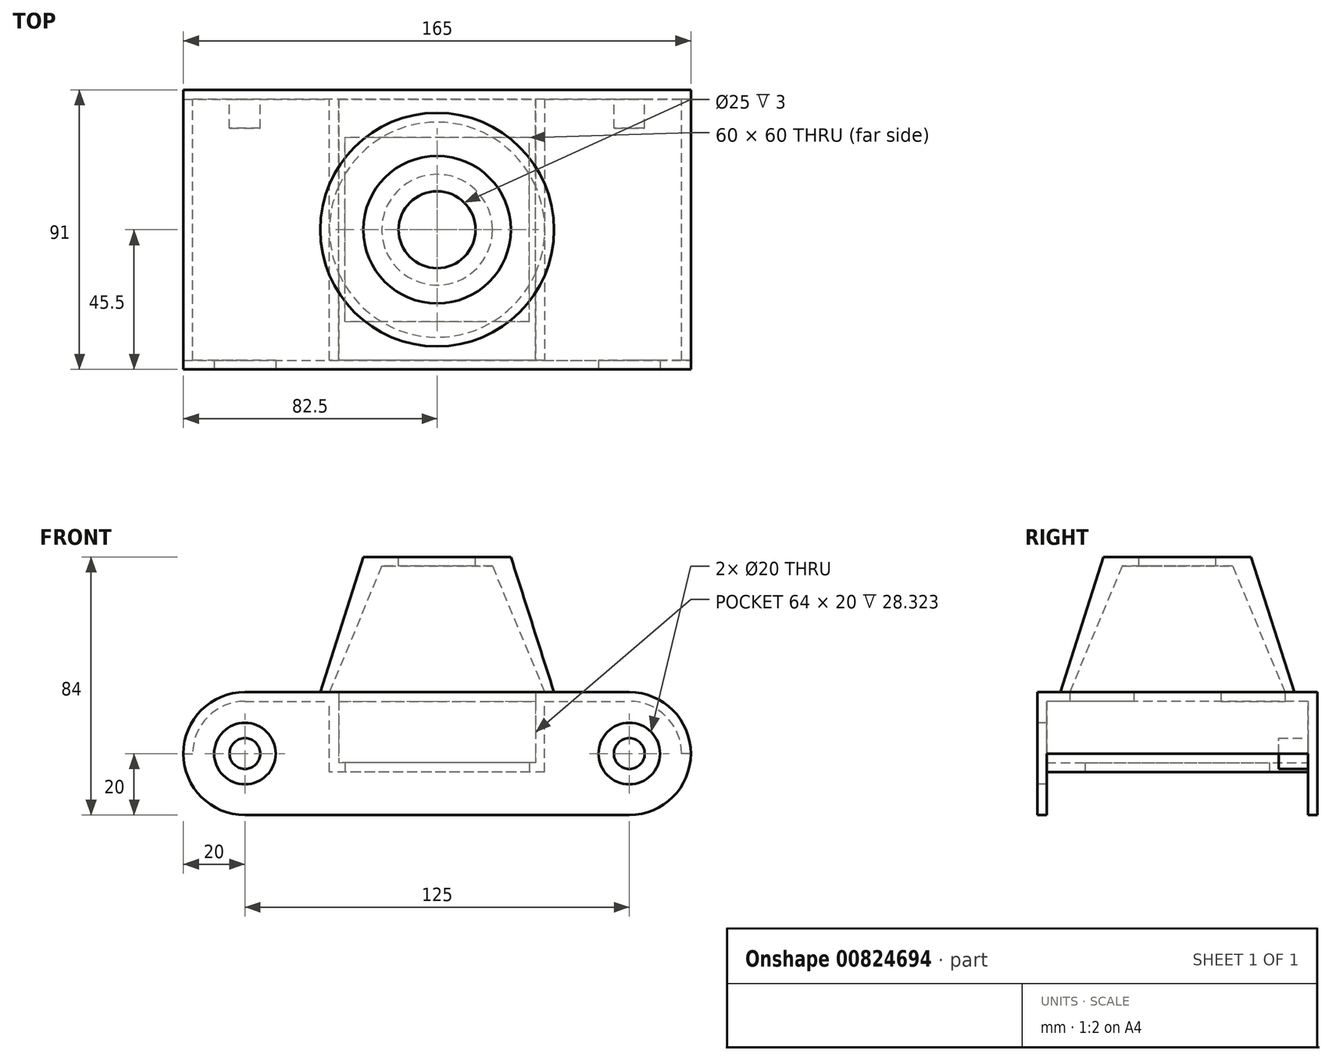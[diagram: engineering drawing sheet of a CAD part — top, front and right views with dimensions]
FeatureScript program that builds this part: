
annotation { "Feature Type Name" : "Feature", "Feature Type Description" : "" }
export const myFeature = defineFeature(function(context is Context, id is Id, definition is map)
    precondition{}
    {
        {
            var Q0;
            Q0=qCreatedBy(makeId("Front.planeOp"),FACE);
            var sketch = newSketch(context, id + "F0", { "sketchPlane" : qUnion([Q0])});
            skLineSegment(sketch, "E0.bottom", {"start": v(62.5, 20) * mm, "end": v(-62.5, 20) * mm});
            skLineSegment(sketch, "E0.top", {"start": v(62.5, -20) * mm, "end": v(-62.5, -20) * mm});
            skLineSegment(sketch, "E0.left", {"start": v(62.5, 20) * mm, "end": v(62.5, -20) * mm});
            skLineSegment(sketch, "E0.right", {"start": v(-62.5, 20) * mm, "end": v(-62.5, -20) * mm});
            skPoint(sketch, "E0.middle", {"position": v(0, 0) * mm});
            skArc(sketch, "E1", {"start": v(-62.5, 20) * mm, "mid": v(-82.5, 0) * mm, "end": v(-62.5, -20) * mm});
            skArc(sketch, "E2", {"start": v(62.5, -20) * mm, "mid": v(82.5, 0) * mm, "end": v(62.5, 20) * mm});
            skSolve(sketch);
        }
        {
            var Q0;
            Q0 = qSketchRegion(id + "F0", true);
            extrude(context, id + "F1", {"entities" : qUnion([Q0]), "depth" : 3 * mm, "offsetDistance" : 25 * mm});
        }
        {
            var Q0;
            Q0=makeQuery(id+"F1.opExtrude","CAP_FACE",FACE,{"disambiguationData":[OSD([sQuery(id+"F0.wireOp",EDGE,"E0.bottom"),sQuery(id+"F0.wireOp",EDGE,"E0.top"),sQuery(id+"F0.wireOp",EDGE,"E1"),sQuery(id+"F0.wireOp",EDGE,"E2")])],"isStart":false});
            var sketch = newSketch(context, id + "F2", { "sketchPlane" : qUnion([Q0])});
            skLineSegment(sketch, "E3.bottom", {"start": v(-62.5, 20) * mm, "end": v(62.5, 20) * mm});
            skLineSegment(sketch, "E3.top", {"start": v(-62.5, 17) * mm, "end": v(62.5, 17) * mm});
            skLineSegment(sketch, "E3.left", {"start": v(-62.5, 20) * mm, "end": v(-62.5, 17) * mm});
            skLineSegment(sketch, "E3.right", {"start": v(62.5, 20) * mm, "end": v(62.5, 17) * mm});
            skLineSegment(sketch, "E4", {"start": v(-82.5, 0) * mm, "end": v(-79.5, 0) * mm});
            skLineSegment(sketch, "E5", {"start": v(82.5, 0) * mm, "end": v(79.5, 0) * mm});
            skArc(sketch, "E6", {"start": v(-62.5, 20) * mm, "mid": v(-76.64, 14.14) * mm, "end": v(-82.5, 0) * mm});
            skArc(sketch, "E7", {"start": v(-62.5, 17) * mm, "mid": v(-74.52, 12.02) * mm, "end": v(-79.5, 0) * mm});
            skArc(sketch, "E8", {"start": v(82.5, 0) * mm, "mid": v(76.64, 14.14) * mm, "end": v(62.5, 20) * mm});
            skArc(sketch, "E9", {"start": v(79.5, 0) * mm, "mid": v(74.52, 12.02) * mm, "end": v(62.5, 17) * mm});
            skSolve(sketch);
        }
        {
            var Q0;
            Q0 = qSketchRegion(id + "F2", true);
            extrude(context, id + "F3", {"entities" : qUnion([Q0]), "operationType" : NewBodyOperationType.ADD, "depth" : 85 * mm, "offsetDistance" : 25 * mm});
        }
        {
            var Q0;
            Q0=makeQuery(id+"F3.opExtrude","CAP_FACE",FACE,{"disambiguationData":[OSD([sQuery(id+"F2.wireOp",EDGE,"E3.bottom"),sQuery(id+"F2.wireOp",EDGE,"E3.top"),sQuery(id+"F2.wireOp",EDGE,"E4"),sQuery(id+"F2.wireOp",EDGE,"E5"),sQuery(id+"F2.wireOp",EDGE,"E6"),sQuery(id+"F2.wireOp",EDGE,"E7"),sQuery(id+"F2.wireOp",EDGE,"E8"),sQuery(id+"F2.wireOp",EDGE,"E9")])],"isStart":false});
            var sketch = newSketch(context, id + "F4", { "sketchPlane" : qUnion([Q0])});
            skLineSegment(sketch, "E10.bottom", {"start": v(-62.5, 20) * mm, "end": v(62.5, 20) * mm});
            skLineSegment(sketch, "E10.top", {"start": v(-62.5, -20) * mm, "end": v(62.5, -20) * mm});
            skLineSegment(sketch, "E10.left", {"start": v(-62.5, 20) * mm, "end": v(-62.5, -20) * mm});
            skLineSegment(sketch, "E10.right", {"start": v(62.5, 20) * mm, "end": v(62.5, -20) * mm});
            skArc(sketch, "E11", {"start": v(-62.5, 20) * mm, "mid": v(-82.5, 0) * mm, "end": v(-62.5, -20) * mm});
            skArc(sketch, "E12", {"start": v(62.5, -20) * mm, "mid": v(82.5, 0) * mm, "end": v(62.5, 20) * mm});
            skSolve(sketch);
        }
        {
            var Q0;
            Q0 = qSketchRegion(id + "F4", true);
            extrude(context, id + "F5", {"entities" : qUnion([Q0]), "operationType" : NewBodyOperationType.ADD, "depth" : 3 * mm, "offsetDistance" : 25 * mm});
        }
        {
            var Q0;
            Q0=makeQuery(id+"F3.opExtrude","SWEPT_FACE",FACE,{"disambiguationData":[OSD([sQuery(id+"F2.wireOp",EDGE,"E3.top")])]});
            var sketch = newSketch(context, id + "F6", { "sketchPlane" : qUnion([Q0])});
            skLineSegment(sketch, "E13", {"start": v(-62.5, 88) * mm, "end": v(62.5, 3) * mm, "construction": true});
            skCircle(sketch, "E14", {"center": v(0, 45.5) * mm, "radius": 35 * mm});
            skSolve(sketch);
        }
        {
            var Q0;
            Q0 = qSketchRegion(id + "F6", true);
            extrude(context, id + "F7", {"entities" : qUnion([Q0]), "operationType" : NewBodyOperationType.REMOVE, "oppositeDirection" : true, "depth" : 25 * mm, "offsetDistance" : 25 * mm});
        }
        {
            var Q0;
            Q0=makeQuery(id+"F5.boolean.opBoolean","MERGE",FACE,{"derivedFrom":[makeQuery(id+"F3.boolean.opBoolean","MERGE",FACE,{"derivedFrom":[makeQuery(id+"F1.opExtrude","SWEPT_FACE",FACE,{"disambiguationData":[OSD([sQuery(id+"F0.wireOp",EDGE,"E0.bottom")])]}),makeQuery(id+"F3.opExtrude","SWEPT_FACE",FACE,{"disambiguationData":[OSD([sQuery(id+"F2.wireOp",EDGE,"E3.bottom")])]})]}),makeQuery(id+"F5.opExtrude","SWEPT_FACE",FACE,{"disambiguationData":[OSD([sQuery(id+"F4.wireOp",EDGE,"E10.bottom")])]})]});
            var sketch = newSketch(context, id + "F8", { "sketchPlane" : qUnion([Q0])});
            skCircle(sketch, "E15", {"center": v(0, -45.5) * mm, "radius": 38 * mm});
            skSolve(sketch);
        }
        {
            var Q0;
            Q0=makeQuery(id+"F8.imprint","IMPRINT",FACE,{"disambiguationData":[TD([[makeQuery(id+"F8.imprint","IMPRINT",EDGE,{"derivedFrom":sQuery(id+"F8.wireOp",EDGE,"E15")}),-1.0]])]});
            cPlane(context, id + "F9", {"entities" : qUnion([Q0]), "cplaneType" : CPlaneType.OFFSET, "offset" : 44 * mm, "width" : 150 * mm, "height" : 150 * mm});
        }
        {
            var Q0;
            Q0=qCreatedBy(id+"F9.planeOp",FACE);
            var sketch = newSketch(context, id + "F10", { "sketchPlane" : qUnion([Q0])});
            skCircle(sketch, "E16", {"center": v(0, -45.5) * mm, "radius": 24 * mm});
            skSolve(sketch);
        }
        {
            var Q1;
            Q1 = qSketchRegion(id + "F10", true);
            var Q2;
            Q2 = qSketchRegion(id + "F8", true);
            loft(context, id + "F11", {"operationType" : NewBodyOperationType.ADD, "sheetProfilesArray" : [{ "sheetProfileEntities" : qUnion([Q1]) }, { "sheetProfileEntities" : qUnion([Q2]) }]});
        }
        {
            var Q0;
            Q0=makeQuery(id+"F11.opLoft","CAP_FACE",FACE,{"disambiguationData":[OSD([makeQuery(id+"F10.imprint","IMPRINT",FACE,{"disambiguationData":[TD([[makeQuery(id+"F10.imprint","IMPRINT",EDGE,{"derivedFrom":sQuery(id+"F10.wireOp",EDGE,"E16")}),1.0]])]})])],"isStart":true});
            var sketch = newSketch(context, id + "F12", { "sketchPlane" : qUnion([Q0])});
            skCircle(sketch, "E17", {"center": v(0, -45.5) * mm, "radius": 12.5 * mm});
            skSolve(sketch);
        }
        {
            var Q0;
            Q0 = qSketchRegion(id + "F12", true);
            extrude(context, id + "F13", {"entities" : qUnion([Q0]), "operationType" : NewBodyOperationType.REMOVE, "oppositeDirection" : true, "depth" : 70.6 * mm, "offsetDistance" : 25 * mm});
        }
        {
            var Q0;
            Q0=makeQuery(id+"F5.boolean.opBoolean","MERGE",FACE,{"derivedFrom":[makeQuery(id+"F3.boolean.opBoolean","MERGE",FACE,{"derivedFrom":[makeQuery(id+"F1.opExtrude","SWEPT_FACE",FACE,{"disambiguationData":[OSD([sQuery(id+"F0.wireOp",EDGE,"E0.bottom")])]}),makeQuery(id+"F3.opExtrude","SWEPT_FACE",FACE,{"disambiguationData":[OSD([sQuery(id+"F2.wireOp",EDGE,"E3.bottom")])]})]}),makeQuery(id+"F5.opExtrude","SWEPT_FACE",FACE,{"disambiguationData":[OSD([sQuery(id+"F4.wireOp",EDGE,"E10.bottom")])]})]});
            var sketch = newSketch(context, id + "F14", { "sketchPlane" : qUnion([Q0])});
            skCircle(sketch, "E18", {"center": v(0, -45.5) * mm, "radius": 35 * mm});
            skSolve(sketch);
        }
        {
            var Q0;
            Q0=qCreatedBy(id+"F9.planeOp",FACE);
            cPlane(context, id + "F15", {"entities" : qUnion([Q0]), "cplaneType" : CPlaneType.OFFSET, "offset" : 3 * mm, "oppositeDirection" : true, "width" : 150 * mm, "height" : 150 * mm});
        }
        {
            var Q0;
            Q0=qCreatedBy(id+"F15.planeOp",FACE);
            var sketch = newSketch(context, id + "F16", { "sketchPlane" : qUnion([Q0])});
            skCircle(sketch, "E19", {"center": v(0, -45.5) * mm, "radius": 18 * mm});
            skSolve(sketch);
        }
        {
            var Q1;
            Q1 = qSketchRegion(id + "F16", true);
            var Q2;
            Q2 = qSketchRegion(id + "F14", true);
            loft(context, id + "F17", {"operationType" : NewBodyOperationType.REMOVE, "sheetProfilesArray" : [{ "sheetProfileEntities" : qUnion([Q1]) }, { "sheetProfileEntities" : qUnion([Q2]) }]});
        }
        {
            var Q0;
            Q0=makeQuery(id+"F1.opExtrude","CAP_FACE",FACE,{"disambiguationData":[OSD([sQuery(id+"F0.wireOp",EDGE,"E0.bottom"),sQuery(id+"F0.wireOp",EDGE,"E0.top"),sQuery(id+"F0.wireOp",EDGE,"E1"),sQuery(id+"F0.wireOp",EDGE,"E2")])],"isStart":false});
            var sketch = newSketch(context, id + "F18", { "sketchPlane" : qUnion([Q0])});
            skLineSegment(sketch, "E20.bottom", {"start": v(35, -6) * mm, "end": v(-35, -6) * mm});
            skLineSegment(sketch, "E20.top", {"start": v(35, -3) * mm, "end": v(-35, -3) * mm});
            skLineSegment(sketch, "E20.left", {"start": v(35, -6) * mm, "end": v(35, -3) * mm});
            skLineSegment(sketch, "E20.right", {"start": v(-35, -6) * mm, "end": v(-35, -3) * mm});
            skPoint(sketch, "E20.middle", {"position": v(0, -4.5) * mm});
            skSolve(sketch);
        }
        {
            var Q0;
            Q0 = qSketchRegion(id + "F18", true);
            extrude(context, id + "F19", {"entities" : qUnion([Q0]), "operationType" : NewBodyOperationType.ADD, "depth" : 85 * mm, "offsetDistance" : 25 * mm});
        }
        {
            var Q0;
            Q0=makeQuery(id+"F19.opExtrude","SWEPT_FACE",FACE,{"disambiguationData":[OSD([sQuery(id+"F18.wireOp",EDGE,"E20.bottom")])]});
            var sketch = newSketch(context, id + "F20", { "sketchPlane" : qUnion([Q0])});
            skLineSegment(sketch, "E21", {"start": v(-35, 88) * mm, "end": v(35, 3) * mm, "construction": true});
            skLineSegment(sketch, "E22.bottom", {"start": v(30, 75.5) * mm, "end": v(-30, 75.5) * mm});
            skLineSegment(sketch, "E22.top", {"start": v(30, 15.5) * mm, "end": v(-30, 15.5) * mm});
            skLineSegment(sketch, "E22.left", {"start": v(30, 75.5) * mm, "end": v(30, 15.5) * mm});
            skLineSegment(sketch, "E22.right", {"start": v(-30, 75.5) * mm, "end": v(-30, 15.5) * mm});
            skPoint(sketch, "E22.middle", {"position": v(0, 45.5) * mm});
            skSolve(sketch);
        }
        {
            var Q0;
            Q0 = qSketchRegion(id + "F20", true);
            extrude(context, id + "F21", {"entities" : qUnion([Q0]), "operationType" : NewBodyOperationType.REMOVE, "oppositeDirection" : true, "depth" : 15.5 * mm, "offsetDistance" : 25 * mm});
        }
        {
            var Q0;
            Q0=makeQuery(id+"F19.opExtrude","SWEPT_FACE",FACE,{"disambiguationData":[OSD([sQuery(id+"F18.wireOp",EDGE,"E20.bottom")])]});
            var sketch = newSketch(context, id + "F22", { "sketchPlane" : qUnion([Q0])});
            skLineSegment(sketch, "E23.bottom", {"start": v(-35, 88) * mm, "end": v(-32, 88) * mm});
            skLineSegment(sketch, "E23.top", {"start": v(-35, 3) * mm, "end": v(-32, 3) * mm});
            skLineSegment(sketch, "E23.left", {"start": v(-35, 88) * mm, "end": v(-35, 3) * mm});
            skLineSegment(sketch, "E23.right", {"start": v(-32, 88) * mm, "end": v(-32, 3) * mm});
            skLineSegment(sketch, "E24.bottom", {"start": v(35, 88) * mm, "end": v(32, 88) * mm});
            skLineSegment(sketch, "E24.top", {"start": v(35, 3) * mm, "end": v(32, 3) * mm});
            skLineSegment(sketch, "E24.left", {"start": v(35, 88) * mm, "end": v(35, 3) * mm});
            skLineSegment(sketch, "E24.right", {"start": v(32, 88) * mm, "end": v(32, 3) * mm});
            skSolve(sketch);
        }
        {
            var Q0;
            Q0 = qSketchRegion(id + "F22", true);
            extrude(context, id + "F23", {"entities" : qUnion([Q0]), "operationType" : NewBodyOperationType.ADD, "oppositeDirection" : true, "depth" : 26 * mm, "offsetDistance" : 25 * mm});
        }
        {
            var Q0;
            {var subQ0=sQuery(id+"F0.wireOp",EDGE,"E0.top");var subQ1=sQuery(id+"F0.wireOp",EDGE,"E2");var subQ2=sQuery(id+"F0.wireOp",EDGE,"E1");Q0=makeQuery(id+"F23.boolean.opBoolean","SPLIT",FACE,{"disambiguationData":[TD([makeQuery(id+"F1.opExtrude","SWEPT_FACE",FACE,{"disambiguationData":[OSD([subQ0])]})])],"derivedFrom":makeQuery(id+"F1.opExtrude","CAP_FACE",FACE,{"disambiguationData":[OSD([sQuery(id+"F0.wireOp",EDGE,"E0.bottom"),subQ0,subQ2,subQ1])],"isStart":false})});}
            var sketch = newSketch(context, id + "F24", { "sketchPlane" : qUnion([Q0])});
            skLineSegment(sketch, "E25", {"start": v(-82.5, 0) * mm, "end": v(82.5, 0) * mm, "construction": true});
            skLineSegment(sketch, "E26", {"start": v(-62.5, 17) * mm, "end": v(-62.5, -20) * mm, "construction": true});
            skLineSegment(sketch, "E27", {"start": v(62.5, -20) * mm, "end": v(62.5, 17) * mm, "construction": true});
            skCircle(sketch, "E28", {"center": v(-62.5, 0) * mm, "radius": 5 * mm});
            skCircle(sketch, "E29", {"center": v(62.5, 0) * mm, "radius": 5 * mm});
            skSolve(sketch);
        }
        {
            var Q0;
            Q0 = qSketchRegion(id + "F24", true);
            extrude(context, id + "F25", {"entities" : qUnion([Q0]), "operationType" : NewBodyOperationType.ADD, "depth" : 9.5 * mm, "offsetDistance" : 25 * mm});
        }
        {
            var Q0;
            Q0=makeQuery(id+"F5.opExtrude","CAP_FACE",FACE,{"disambiguationData":[OSD([sQuery(id+"F4.wireOp",EDGE,"E10.bottom"),sQuery(id+"F4.wireOp",EDGE,"E10.top"),sQuery(id+"F4.wireOp",EDGE,"E11"),sQuery(id+"F4.wireOp",EDGE,"E12")])],"isStart":false});
            var sketch = newSketch(context, id + "F26", { "sketchPlane" : qUnion([Q0])});
            skLineSegment(sketch, "E30", {"start": v(-82.5, 0) * mm, "end": v(82.5, 0) * mm, "construction": true});
            skLineSegment(sketch, "E31", {"start": v(62.5, -20) * mm, "end": v(62.5, 20) * mm, "construction": true});
            skLineSegment(sketch, "E32", {"start": v(-62.5, -20) * mm, "end": v(-62.5, 20) * mm, "construction": true});
            skCircle(sketch, "E33", {"center": v(-62.5, 0) * mm, "radius": 10 * mm});
            skCircle(sketch, "E34", {"center": v(62.5, 0) * mm, "radius": 10 * mm});
            skSolve(sketch);
        }
        {
            var Q0;
            Q0 = qSketchRegion(id + "F26", true);
            extrude(context, id + "F27", {"entities" : qUnion([Q0]), "operationType" : NewBodyOperationType.REMOVE, "oppositeDirection" : true, "depth" : 25 * mm, "offsetDistance" : 25 * mm});
        }
    });
